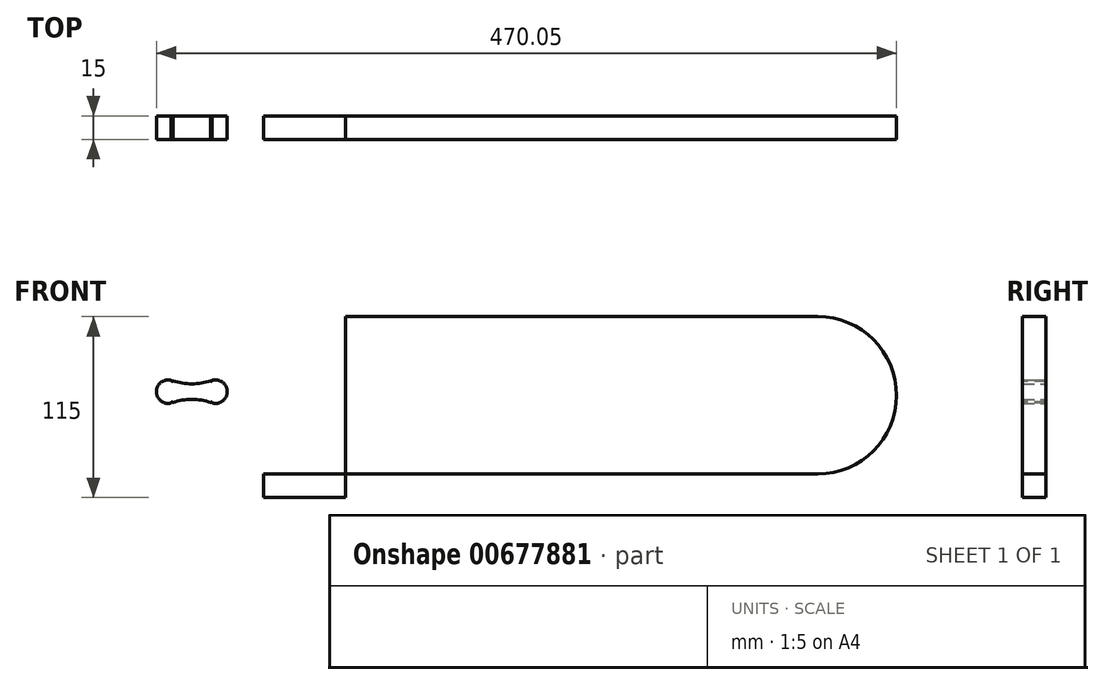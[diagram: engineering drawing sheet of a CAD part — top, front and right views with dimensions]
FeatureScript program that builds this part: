
annotation { "Feature Type Name" : "Feature", "Feature Type Description" : "" }
export const myFeature = defineFeature(function(context is Context, id is Id, definition is map)
    precondition{}
    {
        {
            assignVariable(context, id + "F0", {"name" : "thickness", "anyValue" : 15 * mm});
        }
        {
            var Q0;
            Q0=qCreatedBy(makeId("Front.planeOp"),FACE);
            var sketch = newSketch(context, id + "F1", { "sketchPlane" : qUnion([Q0])});
            skLineSegment(sketch, "E0.bottom", {"start": v(0, 0) * mm, "end": v(300, 0) * mm});
            skLineSegment(sketch, "E0.top", {"start": v(0, 100) * mm, "end": v(300, 100) * mm});
            skLineSegment(sketch, "E0.left", {"start": v(0, 0) * mm, "end": v(0, 100) * mm});
            skLineSegment(sketch, "E0.right", {"start": v(300, 0) * mm, "end": v(300, 100) * mm});
            skCircle(sketch, "E1", {"center": v(300, 50) * mm, "radius": 50 * mm});
            skSolve(sketch);
        }
        {
            var Q0;
            Q0 = qSketchRegion(id + "F1", true);
            extrude(context, id + "F2", {"entities" : qUnion([Q0]), "depth" : getVariable(context, 'thickness'), "offsetDistance" : 25 * mm, "symmetric" : true});
        }
        {
            var Q0;
            Q0=qCreatedBy(makeId("Front.planeOp"),FACE);
            var sketch = newSketch(context, id + "F3", { "sketchPlane" : qUnion([Q0])});
            skLineSegment(sketch, "E2.bottom", {"start": v(-52.01, 0) * mm, "end": v(0, 0) * mm});
            skLineSegment(sketch, "E2.top", {"start": v(-52.01, -15) * mm, "end": v(0, -15) * mm});
            skLineSegment(sketch, "E2.left", {"start": v(0, 0) * mm, "end": v(0, -15) * mm});
            skLineSegment(sketch, "E2.right", {"start": v(-52.01, 0) * mm, "end": v(-52.01, -15) * mm});
            skSolve(sketch);
        }
        {
            var Q0;
            Q0 = qSketchRegion(id + "F3", true);
            extrude(context, id + "F4", {"entities" : qUnion([Q0]), "depth" : getVariable(context, 'thickness'), "offsetDistance" : 25 * mm, "symmetric" : true});
        }
        {
            var Q0;
            Q0=qCreatedBy(makeId("Front.planeOp"),FACE);
            var sketch = newSketch(context, id + "F5", { "sketchPlane" : qUnion([Q0])});
            skLineSegment(sketch, "E3", {"start": v(-82.55, 52.33) * mm, "end": v(-112.55, 52.33) * mm, "construction": true});
            skCircle(sketch, "E4", {"center": v(-112.55, 52.33) * mm, "radius": 7.5 * mm});
            skCircle(sketch, "E5", {"center": v(-82.55, 52.33) * mm, "radius": 7.5 * mm});
            skCircle(sketch, "E6", {"center": v(-97.55, 94.76) * mm, "radius": 37.5 * mm});
            skPoint(sketch, "E6.centerSnap0", {"position": v(-97.55, 52.33) * mm});
            skCircle(sketch, "E7", {"center": v(-97.55, 9.9) * mm, "radius": 37.5 * mm});
            skSolve(sketch);
        }
        {
            var Q0;
            {var subQ0=sQuery(id+"F5.wireOp",EDGE,"E4");var subQ1=makeQuery(id+"F5.imprint","INTERSECT",VERTEX,{"derivedFrom":[subQ0,sQuery(id+"F5.wireOp",EDGE,"E6")]});Q0=makeQuery(id+"F5.imprint","IMPRINT",FACE,{"disambiguationData":[TD([[makeQuery(id+"F5.imprint","IMPRINT",EDGE,{"disambiguationData":[TD([[subQ1,-1.0]])],"derivedFrom":subQ0}),1.0]])]});}
            var Q1;
            {var subQ0=sQuery(id+"F5.wireOp",EDGE,"E6");var subQ1=sQuery(id+"F5.wireOp",EDGE,"E4");var subQ2=makeQuery(id+"F5.imprint","INTERSECT",VERTEX,{"derivedFrom":[subQ1,subQ0]});Q1=makeQuery(id+"F5.imprint","IMPRINT",FACE,{"disambiguationData":[TD([[makeQuery(id+"F5.imprint","IMPRINT",EDGE,{"disambiguationData":[TD([[subQ2,1.0]])],"derivedFrom":subQ1}),-1.0]])]});}
            var Q2;
            {var subQ0=sQuery(id+"F5.wireOp",EDGE,"E5");var subQ1=makeQuery(id+"F5.imprint","INTERSECT",VERTEX,{"derivedFrom":[subQ0,sQuery(id+"F5.wireOp",EDGE,"E6")]});Q2=makeQuery(id+"F5.imprint","IMPRINT",FACE,{"disambiguationData":[TD([[makeQuery(id+"F5.imprint","IMPRINT",EDGE,{"disambiguationData":[TD([[subQ1,-1.0]])],"derivedFrom":subQ0}),1.0]])]});}
            extrude(context, id + "F6", {"entities" : qUnion([Q0, Q1, Q2]), "depth" : getVariable(context, 'thickness'), "offsetDistance" : 25 * mm, "symmetric" : true});
        }
        {
            var Q0;
            Q0=makeQuery(id+"F6.opExtrude","CAP_FACE",FACE,{"disambiguationData":[OSD([sQuery(id+"F5.wireOp",EDGE,"E4"),sQuery(id+"F5.wireOp",EDGE,"E5"),sQuery(id+"F5.wireOp",EDGE,"E6"),sQuery(id+"F5.wireOp",EDGE,"E7")])],"isStart":false});
            var sketch = newSketch(context, id + "F7", { "sketchPlane" : qUnion([Q0])});
            skCircle(sketch, "E8", {"center": v(-110.05, 59.4) * mm, "radius": 0.5 * mm});
            skCircle(sketch, "E9", {"center": v(-85.05, 59.4) * mm, "radius": 0.5 * mm});
            skCircle(sketch, "E10", {"center": v(-85.05, 45.26) * mm, "radius": 0.5 * mm});
            skCircle(sketch, "E11", {"center": v(-110.05, 45.26) * mm, "radius": 0.5 * mm});
            skSolve(sketch);
        }
        {
            var Q0;
            Q0 = qSketchRegion(id + "F7", true);
            extrude(context, id + "F8", {"entities" : qUnion([Q0]), "operationType" : NewBodyOperationType.REMOVE, "oppositeDirection" : true, "depth" : 25 * mm, "offsetDistance" : 25 * mm});
        }
    });
